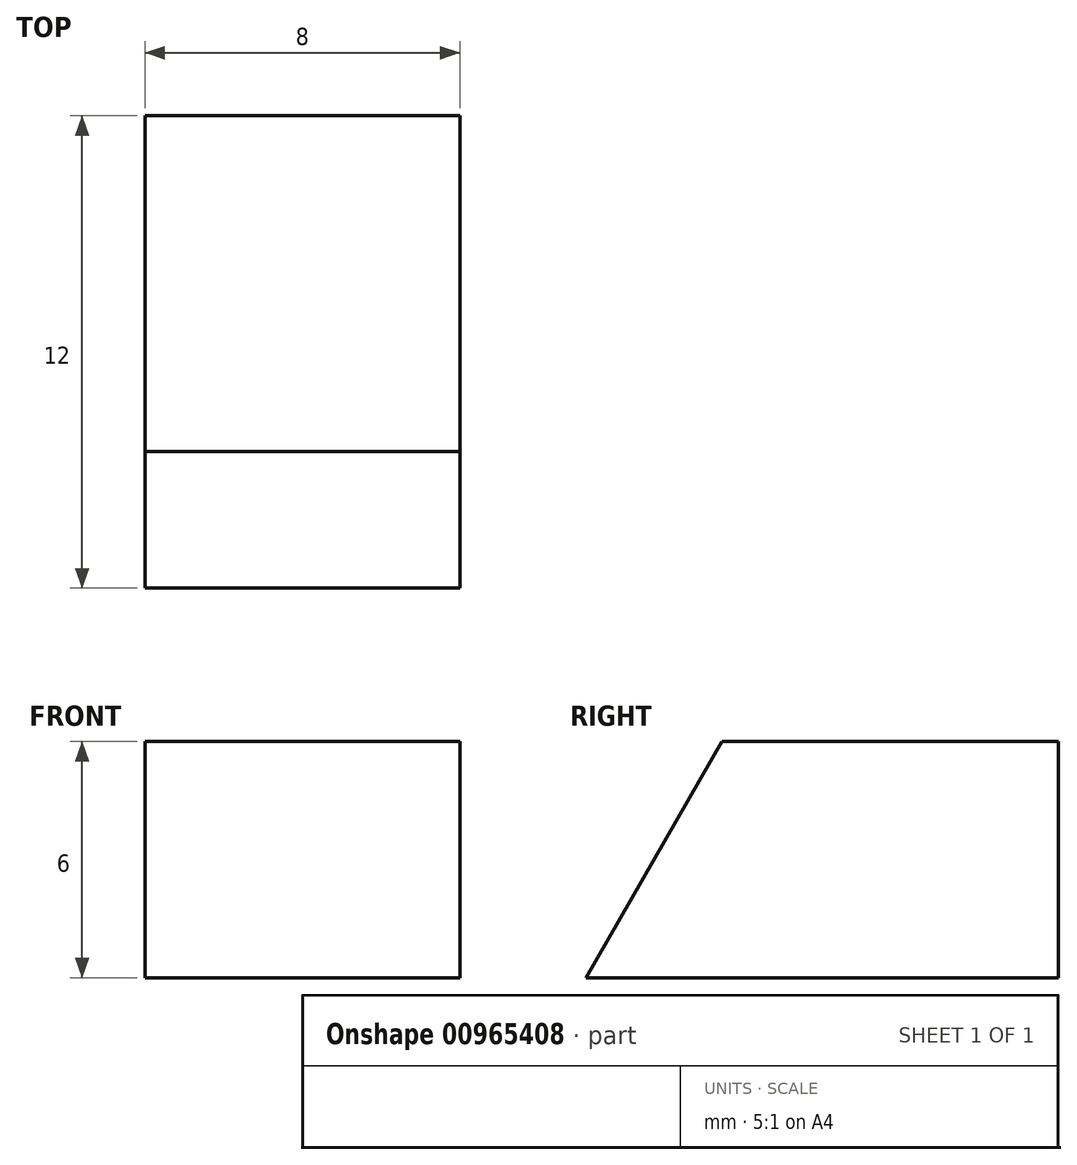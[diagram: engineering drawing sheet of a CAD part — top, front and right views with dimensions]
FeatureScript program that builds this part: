
annotation { "Feature Type Name" : "Feature", "Feature Type Description" : "" }
export const myFeature = defineFeature(function(context is Context, id is Id, definition is map)
    precondition{}
    {
        {
            var Q0;
            Q0=qCreatedBy(makeId("Front.planeOp"),FACE);
            var sketch = newSketch(context, id + "F0", { "sketchPlane" : qUnion([Q0])});
            skLineSegment(sketch, "E0.bottom", {"start": v(4, 3) * mm, "end": v(-4, 3) * mm});
            skLineSegment(sketch, "E0.top", {"start": v(4, -3) * mm, "end": v(-4, -3) * mm});
            skLineSegment(sketch, "E0.left", {"start": v(4, 3) * mm, "end": v(4, -3) * mm});
            skLineSegment(sketch, "E0.right", {"start": v(-4, 3) * mm, "end": v(-4, -3) * mm});
            skPoint(sketch, "E0.middle", {"position": v(0, 0) * mm});
            skSolve(sketch);
        }
        {
            var Q0;
            Q0=makeQuery(id+"F0.imprint","IMPRINT",FACE,{"disambiguationData":[TD([[makeQuery(id+"F0.imprint","IMPRINT",EDGE,{"derivedFrom":sQuery(id+"F0.wireOp",EDGE,"E0.bottom")}),1.0]])]});
            extrude(context, id + "F1", {"entities" : qUnion([Q0]), "depth" : 12 * mm, "offsetDistance" : 25 * mm});
        }
        {
            var Q0;
            Q0=makeQuery(id+"F1.opExtrude","SWEPT_FACE",FACE,{"disambiguationData":[OSD([sQuery(id+"F0.wireOp",EDGE,"E0.left")])]});
            var sketch = newSketch(context, id + "F2", { "sketchPlane" : qUnion([Q0])});
            skLineSegment(sketch, "E1", {"start": v(-12, -3) * mm, "end": v(-8.54, 3) * mm});
            skSolve(sketch);
        }
        {
            var Q0;
            {var subQ0=sQuery(id+"F2.wireOp",EDGE,"E1");Q0=makeQuery(id+"F2.imprint","IMPRINT",FACE,{"disambiguationData":[TD([[makeQuery(id+"F2.imprint","IMPRINT",EDGE,{"derivedFrom":subQ0}),1.0]])]});}
            extrude(context, id + "F3", {"entities" : qUnion([Q0]), "operationType" : NewBodyOperationType.REMOVE, "endBound" : BoundingType.THROUGH_ALL, "oppositeDirection" : true, "depth" : 25 * mm, "offsetDistance" : 25 * mm});
        }
    });
